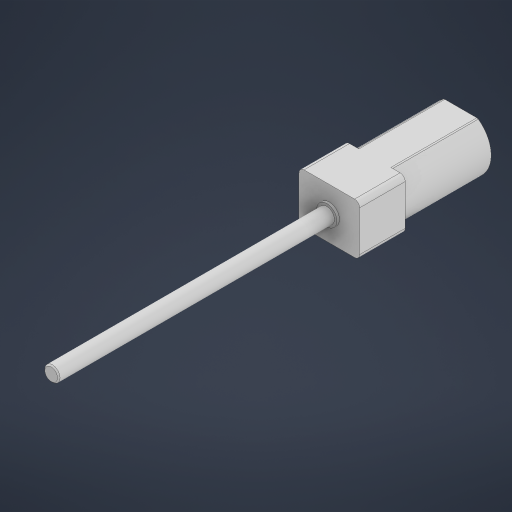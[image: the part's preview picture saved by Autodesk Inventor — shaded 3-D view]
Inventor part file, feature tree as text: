
AUTODESK INVENTOR PART (.ipt)
format: ipt  version: 2023.4 (Build 274418000, 418)  size: 226,816 bytes
history: native  units: mm
features: extrude x4, sketch x3, fillet x2, chamfer x1, projected_geometry x1
ambient origin geometry x8: Origin, YZ Plane, XZ Plane, XY Plane, X Axis, Y Axis, Z Axis, Center Point
bodies: Solid1 (feature_tree)
feature tree (11):
  extrude  "Extrusion1"  Depth=10.0mm
  sketch  "Sketch2"  dims[d2=26.0mm d3=0.0mm d4=3.0mm d5=55.0mm d6=0.0mm]
  extrude  "Extrusion2"  Depth=55.0mm
  fillet  "Fillet1"  Radius=55.0mm
  extrude  "Extrusion3"  Depth=12.0mm
  fillet  "Fillet2"  Radius=17.0mm
  extrude  "Extrusion4"  Depth=0.5mm
  chamfer  "Chamfer1"  Distance=4.0mm
  sketch  "Sketch1"  dims[d0=12.0mm d1=10.0mm]
  sketch  "Sketch3"  dims[d7=1.0mm d8=12.0mm d9=17.0mm d10=0.0mm d11=0.5mm d12=4.0mm d13=0.5mm d14=0.0mm d15=0.25mm d16=2.0mm d17=45.0deg]
  projected_geometry  "Projected Loop1"
